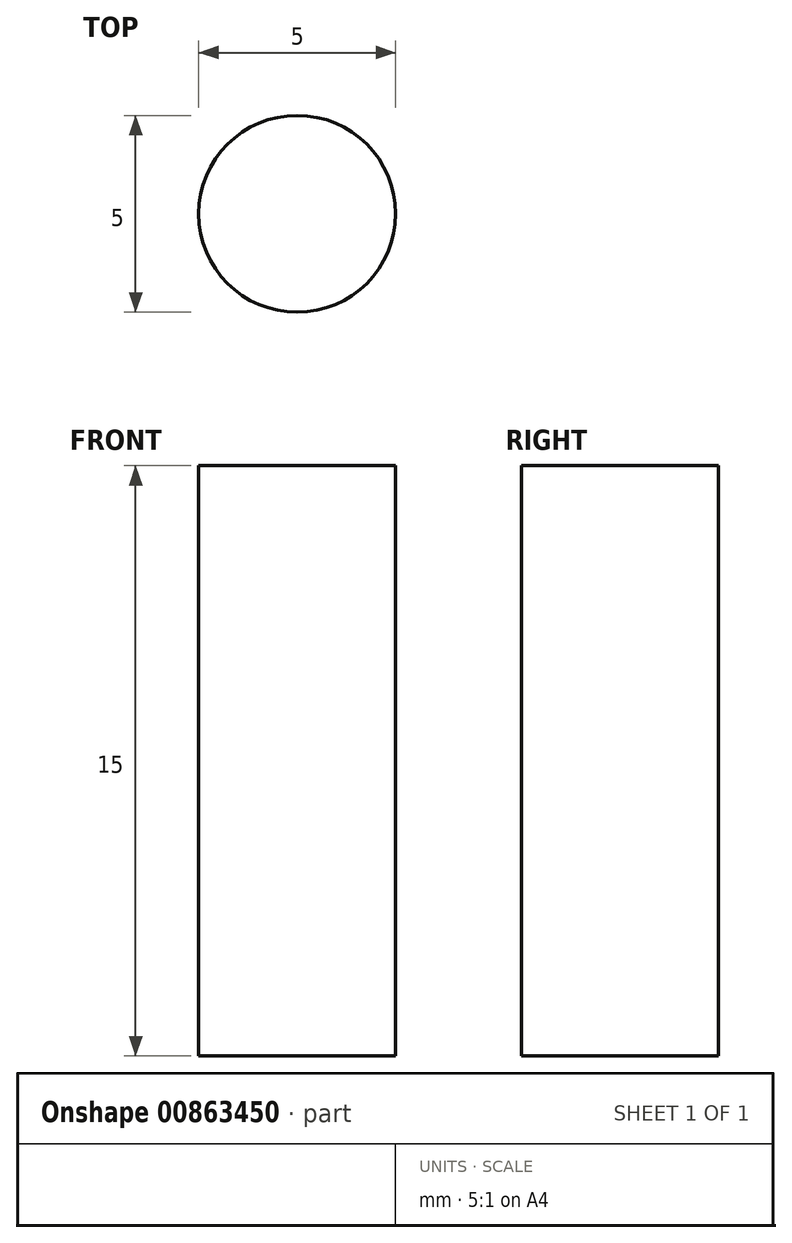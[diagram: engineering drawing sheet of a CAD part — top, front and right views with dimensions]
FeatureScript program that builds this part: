
annotation { "Feature Type Name" : "Feature", "Feature Type Description" : "" }
export const myFeature = defineFeature(function(context is Context, id is Id, definition is map)
    precondition{}
    {
        {
            var Q0;
            Q0=qCreatedBy(makeId("Top.planeOp"),FACE);
            var sketch = newSketch(context, id + "F0", { "sketchPlane" : qUnion([Q0])});
            skCircle(sketch, "E0", {"center": v(0, 0) * mm, "radius": 2.5 * mm});
            skSolve(sketch);
        }
        {
            var Q0;
            Q0=makeQuery(id+"F0.imprint","IMPRINT",FACE,{"disambiguationData":[TD([[makeQuery(id+"F0.imprint","IMPRINT",EDGE,{"derivedFrom":sQuery(id+"F0.wireOp",EDGE,"E0")}),1.0]])]});
            extrude(context, id + "F1", {"entities" : qUnion([Q0]), "depth" : 15 * mm, "offsetDistance" : 25 * mm});
        }
    });
